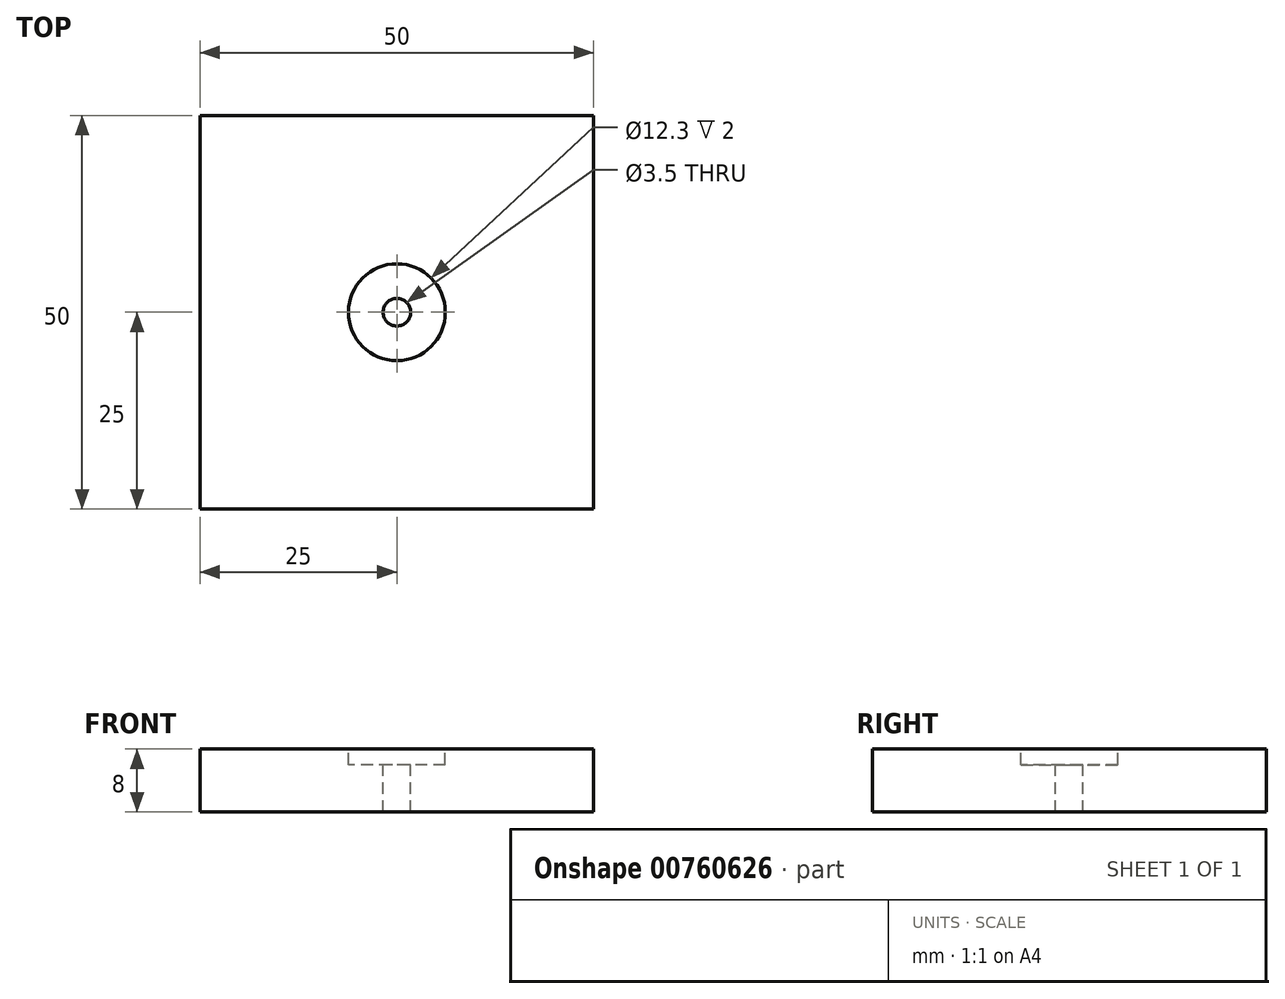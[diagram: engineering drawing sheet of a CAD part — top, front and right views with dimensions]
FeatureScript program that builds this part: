
annotation { "Feature Type Name" : "Feature", "Feature Type Description" : "" }
export const myFeature = defineFeature(function(context is Context, id is Id, definition is map)
    precondition{}
    {
        {
            var Q0;
            Q0=qCreatedBy(makeId("Top.planeOp"),FACE);
            var sketch = newSketch(context, id + "F0", { "sketchPlane" : qUnion([Q0])});
            skLineSegment(sketch, "E0.bottom", {"start": v(-25, 25) * mm, "end": v(25, 25) * mm});
            skLineSegment(sketch, "E0.top", {"start": v(-25, -25) * mm, "end": v(25, -25) * mm});
            skLineSegment(sketch, "E0.left", {"start": v(-25, 25) * mm, "end": v(-25, -25) * mm});
            skLineSegment(sketch, "E0.right", {"start": v(25, 25) * mm, "end": v(25, -25) * mm});
            skPoint(sketch, "E0.middle", {"position": v(0, 0) * mm});
            skSolve(sketch);
        }
        {
            var Q0;
            Q0=makeQuery(id+"F0.imprint","IMPRINT",FACE,{"disambiguationData":[TD([[makeQuery(id+"F0.imprint","IMPRINT",EDGE,{"derivedFrom":sQuery(id+"F0.wireOp",EDGE,"E0.bottom")}),-1.0]])]});
            extrude(context, id + "F1", {"entities" : qUnion([Q0]), "oppositeDirection" : true, "depth" : 8 * mm, "offsetDistance" : 25 * mm});
        }
        {
            var Q0;
            Q0=makeQuery(id+"F1.opExtrude","CAP_FACE",FACE,{"disambiguationData":[OSD([sQuery(id+"F0.wireOp",EDGE,"E0.bottom"),sQuery(id+"F0.wireOp",EDGE,"E0.top"),sQuery(id+"F0.wireOp",EDGE,"E0.left"),sQuery(id+"F0.wireOp",EDGE,"E0.right")])],"isStart":true});
            var sketch = newSketch(context, id + "F2", { "sketchPlane" : qUnion([Q0])});
            skCircle(sketch, "E1", {"center": v(0, 0) * mm, "radius": 6.15 * mm});
            skSolve(sketch);
        }
        {
            var Q0;
            Q0=qSketchRegion(id+"F2",true);
            extrude(context, id + "F3", {"entities" : qUnion([Q0]), "operationType" : NewBodyOperationType.REMOVE, "oppositeDirection" : true, "depth" : 2 * mm, "offsetDistance" : 25 * mm});
        }
        {
            var Q0;
            Q0=makeQuery(id+"F3.boolean.opBoolean","COPY",FACE,{"derivedFrom":makeQuery(id+"F3.opExtrude","CAP_FACE",FACE,{"disambiguationData":[OSD([sQuery(id+"F2.wireOp",EDGE,"E1")])],"isStart":false})});
            var sketch = newSketch(context, id + "F4", { "sketchPlane" : qUnion([Q0])});
            skCircle(sketch, "E2", {"center": v(0, 0) * mm, "radius": 1.75 * mm});
            skSolve(sketch);
        }
        {
            var Q0;
            Q0=qSketchRegion(id+"F4",true);
            extrude(context, id + "F5", {"entities" : qUnion([Q0]), "operationType" : NewBodyOperationType.REMOVE, "endBound" : BoundingType.THROUGH_ALL, "oppositeDirection" : true, "depth" : 25 * mm, "offsetDistance" : 25 * mm});
        }
    });
